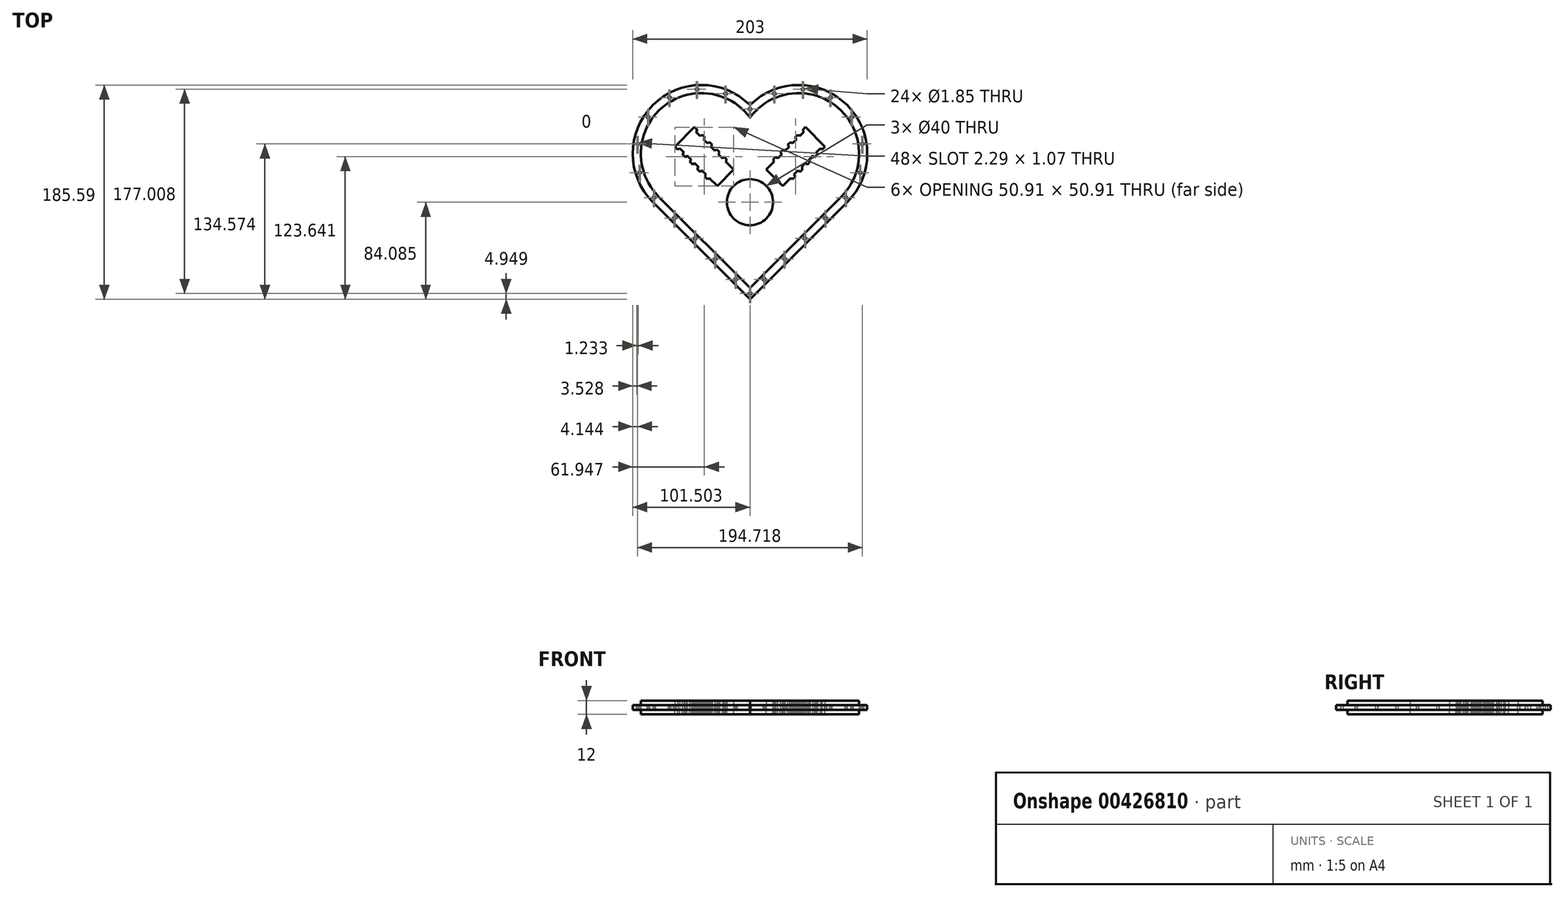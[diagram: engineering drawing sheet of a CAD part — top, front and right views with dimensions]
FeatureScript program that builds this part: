
annotation { "Feature Type Name" : "Feature", "Feature Type Description" : "" }
export const myFeature = defineFeature(function(context is Context, id is Id, definition is map)
    precondition{}
    {
        {
            var Q0;
            Q0=qCreatedBy(makeId("Top.planeOp"),FACE);
            var sketch = newSketch(context, id + "F0", { "sketchPlane" : qUnion([Q0])});
            skArc(sketch, "E0", {"start": v(87.8, -88.57) * mm, "mid": v(87.8, -4.49) * mm, "end": v(3.72, -4.49) * mm});
            skArc(sketch, "E1.MirrorCS", {"start": v(-80.36, -88.57) * mm, "mid": v(-80.36, -4.49) * mm, "end": v(3.72, -4.49) * mm});
            skLineSegment(sketch, "E2", {"start": v(87.8, -88.57) * mm, "end": v(3.72, -172.66) * mm});
            skLineSegment(sketch, "E3", {"start": v(3.72, -172.66) * mm, "end": v(-80.36, -88.57) * mm});
            skCircle(sketch, "E4", {"center": v(3.72, -7.99) * mm, "radius": 0.93 * mm});
            skArc(sketch, "E5", {"start": v(3.64, -6.94) * mm, "mid": v(2.67, -7.99) * mm, "end": v(3.64, -9.04) * mm});
            skArc(sketch, "E6.trimOffspring", {"start": v(3.8, -9.04) * mm, "mid": v(4.77, -7.99) * mm, "end": v(3.8, -6.94) * mm});
            skArc(sketch, "E7.0", {"start": v(3.63, -6.84) * mm, "mid": v(2.57, -7.99) * mm, "end": v(3.63, -9.14) * mm});
            skArc(sketch, "E8.0", {"start": v(3.81, -9.14) * mm, "mid": v(4.87, -7.99) * mm, "end": v(3.81, -6.84) * mm});
            skLineSegment(sketch, "E9", {"start": v(3.8, -9.04) * mm, "end": v(3.81, -9.14) * mm});
            skLineSegment(sketch, "E10", {"start": v(3.64, -9.04) * mm, "end": v(3.63, -9.14) * mm});
            skLineSegment(sketch, "E11", {"start": v(3.63, -6.84) * mm, "end": v(3.64, -6.94) * mm});
            skLineSegment(sketch, "E12", {"start": v(3.81, -6.84) * mm, "end": v(3.8, -6.94) * mm});
            skCircle(sketch, "E13", {"center": v(24.85, 5.37) * mm, "radius": 0.93 * mm});
            skArc(sketch, "E14", {"start": v(24.77, 6.42) * mm, "mid": v(23.8, 5.37) * mm, "end": v(24.77, 4.32) * mm});
            skArc(sketch, "E15.trimOffspring", {"start": v(24.94, 4.32) * mm, "mid": v(25.9, 5.37) * mm, "end": v(24.94, 6.42) * mm});
            skArc(sketch, "E16.0", {"start": v(24.76, 6.52) * mm, "mid": v(23.7, 5.37) * mm, "end": v(24.76, 4.22) * mm});
            skArc(sketch, "E17.0", {"start": v(24.94, 4.22) * mm, "mid": v(26, 5.37) * mm, "end": v(24.94, 6.52) * mm});
            skLineSegment(sketch, "E18", {"start": v(24.94, 4.32) * mm, "end": v(24.94, 4.22) * mm});
            skLineSegment(sketch, "E19", {"start": v(24.77, 4.32) * mm, "end": v(24.76, 4.22) * mm});
            skLineSegment(sketch, "E20", {"start": v(24.76, 6.52) * mm, "end": v(24.77, 6.42) * mm});
            skLineSegment(sketch, "E21", {"start": v(24.94, 6.52) * mm, "end": v(24.94, 6.42) * mm});
            skCircle(sketch, "E22", {"center": v(49.54, 9.3) * mm, "radius": 0.93 * mm});
            skArc(sketch, "E23", {"start": v(49.46, 10.34) * mm, "mid": v(48.5, 9.3) * mm, "end": v(49.46, 8.25) * mm});
            skArc(sketch, "E24.trimOffspring", {"start": v(49.63, 8.25) * mm, "mid": v(50.6, 9.3) * mm, "end": v(49.63, 10.34) * mm});
            skArc(sketch, "E25.0", {"start": v(49.45, 10.44) * mm, "mid": v(48.4, 9.3) * mm, "end": v(49.45, 8.15) * mm});
            skArc(sketch, "E26.0", {"start": v(49.63, 8.15) * mm, "mid": v(50.7, 9.3) * mm, "end": v(49.63, 10.44) * mm});
            skLineSegment(sketch, "E27", {"start": v(49.63, 8.25) * mm, "end": v(49.63, 8.15) * mm});
            skLineSegment(sketch, "E28", {"start": v(49.46, 8.25) * mm, "end": v(49.45, 8.15) * mm});
            skLineSegment(sketch, "E29", {"start": v(49.45, 10.44) * mm, "end": v(49.46, 10.34) * mm});
            skLineSegment(sketch, "E30", {"start": v(49.63, 10.44) * mm, "end": v(49.63, 10.34) * mm});
            skCircle(sketch, "E31", {"center": v(73.48, 2.08) * mm, "radius": 0.93 * mm});
            skArc(sketch, "E32", {"start": v(73.4, 3.13) * mm, "mid": v(72.43, 2.08) * mm, "end": v(73.4, 1.03) * mm});
            skArc(sketch, "E33.trimOffspring", {"start": v(73.56, 1.03) * mm, "mid": v(74.53, 2.08) * mm, "end": v(73.56, 3.13) * mm});
            skArc(sketch, "E34.0", {"start": v(73.39, 3.23) * mm, "mid": v(72.33, 2.08) * mm, "end": v(73.39, 0.93) * mm});
            skArc(sketch, "E35.0", {"start": v(73.57, 0.93) * mm, "mid": v(74.63, 2.08) * mm, "end": v(73.57, 3.23) * mm});
            skLineSegment(sketch, "E36", {"start": v(73.56, 1.03) * mm, "end": v(73.57, 0.93) * mm});
            skLineSegment(sketch, "E37", {"start": v(73.4, 1.03) * mm, "end": v(73.39, 0.93) * mm});
            skLineSegment(sketch, "E38", {"start": v(73.39, 3.23) * mm, "end": v(73.4, 3.13) * mm});
            skLineSegment(sketch, "E39", {"start": v(73.57, 3.23) * mm, "end": v(73.56, 3.13) * mm});
            skCircle(sketch, "E40", {"center": v(91.88, -14.84) * mm, "radius": 0.93 * mm});
            skArc(sketch, "E41", {"start": v(91.8, -13.8) * mm, "mid": v(90.83, -14.84) * mm, "end": v(91.8, -15.89) * mm});
            skArc(sketch, "E42.trimOffspring", {"start": v(91.97, -15.89) * mm, "mid": v(92.93, -14.84) * mm, "end": v(91.97, -13.8) * mm});
            skArc(sketch, "E43.0", {"start": v(91.8, -13.7) * mm, "mid": v(90.73, -14.84) * mm, "end": v(91.8, -15.99) * mm});
            skArc(sketch, "E44.0", {"start": v(91.97, -15.99) * mm, "mid": v(93.03, -14.84) * mm, "end": v(91.97, -13.7) * mm});
            skLineSegment(sketch, "E45", {"start": v(91.97, -15.89) * mm, "end": v(91.97, -15.99) * mm});
            skLineSegment(sketch, "E46", {"start": v(91.8, -15.89) * mm, "end": v(91.8, -15.99) * mm});
            skLineSegment(sketch, "E47", {"start": v(91.8, -13.7) * mm, "end": v(91.8, -13.8) * mm});
            skLineSegment(sketch, "E48", {"start": v(91.97, -13.7) * mm, "end": v(91.97, -13.8) * mm});
            skCircle(sketch, "E49", {"center": v(101.08, -38.09) * mm, "radius": 0.93 * mm});
            skArc(sketch, "E50", {"start": v(101, -37.04) * mm, "mid": v(100.03, -38.09) * mm, "end": v(101, -39.13) * mm});
            skArc(sketch, "E51.trimOffspring", {"start": v(101.16, -39.13) * mm, "mid": v(102.13, -38.09) * mm, "end": v(101.16, -37.04) * mm});
            skArc(sketch, "E52.0", {"start": v(101, -36.94) * mm, "mid": v(99.93, -38.09) * mm, "end": v(101, -39.23) * mm});
            skArc(sketch, "E53.0", {"start": v(101.17, -39.23) * mm, "mid": v(102.23, -38.09) * mm, "end": v(101.17, -36.94) * mm});
            skLineSegment(sketch, "E54", {"start": v(101.16, -39.13) * mm, "end": v(101.17, -39.23) * mm});
            skLineSegment(sketch, "E55", {"start": v(101, -39.13) * mm, "end": v(101, -39.23) * mm});
            skLineSegment(sketch, "E56", {"start": v(101, -36.94) * mm, "end": v(101, -37.04) * mm});
            skLineSegment(sketch, "E57", {"start": v(101.17, -36.94) * mm, "end": v(101.16, -37.04) * mm});
            skCircle(sketch, "E58", {"center": v(99.24, -63.02) * mm, "radius": 0.93 * mm});
            skArc(sketch, "E59", {"start": v(99.16, -61.97) * mm, "mid": v(98.19, -63.02) * mm, "end": v(99.16, -64.06) * mm});
            skArc(sketch, "E60.trimOffspring", {"start": v(99.32, -64.06) * mm, "mid": v(100.29, -63.02) * mm, "end": v(99.32, -61.97) * mm});
            skArc(sketch, "E61.0", {"start": v(99.15, -61.87) * mm, "mid": v(98.09, -63.02) * mm, "end": v(99.15, -64.16) * mm});
            skArc(sketch, "E62.0", {"start": v(99.33, -64.16) * mm, "mid": v(100.39, -63.02) * mm, "end": v(99.33, -61.87) * mm});
            skLineSegment(sketch, "E63", {"start": v(99.32, -64.06) * mm, "end": v(99.33, -64.16) * mm});
            skLineSegment(sketch, "E64", {"start": v(99.16, -64.06) * mm, "end": v(99.15, -64.16) * mm});
            skLineSegment(sketch, "E65", {"start": v(99.15, -61.87) * mm, "end": v(99.16, -61.97) * mm});
            skLineSegment(sketch, "E66", {"start": v(99.33, -61.87) * mm, "end": v(99.32, -61.97) * mm});
            skCircle(sketch, "E67", {"center": v(86.72, -84.66) * mm, "radius": 0.93 * mm});
            skArc(sketch, "E68", {"start": v(86.64, -83.61) * mm, "mid": v(85.67, -84.66) * mm, "end": v(86.64, -85.7) * mm});
            skArc(sketch, "E69.trimOffspring", {"start": v(86.8, -85.7) * mm, "mid": v(87.77, -84.66) * mm, "end": v(86.8, -83.61) * mm});
            skArc(sketch, "E70.0", {"start": v(86.63, -83.51) * mm, "mid": v(85.57, -84.66) * mm, "end": v(86.63, -85.8) * mm});
            skArc(sketch, "E71.0", {"start": v(86.81, -85.8) * mm, "mid": v(87.87, -84.66) * mm, "end": v(86.81, -83.51) * mm});
            skLineSegment(sketch, "E72", {"start": v(86.8, -85.7) * mm, "end": v(86.81, -85.8) * mm});
            skLineSegment(sketch, "E73", {"start": v(86.64, -85.7) * mm, "end": v(86.63, -85.8) * mm});
            skLineSegment(sketch, "E74", {"start": v(86.63, -83.51) * mm, "end": v(86.64, -83.61) * mm});
            skLineSegment(sketch, "E75", {"start": v(86.81, -83.51) * mm, "end": v(86.8, -83.61) * mm});
            skCircle(sketch, "E76", {"center": v(69.07, -102.36) * mm, "radius": 0.93 * mm});
            skArc(sketch, "E77", {"start": v(68.99, -101.32) * mm, "mid": v(68.02, -102.36) * mm, "end": v(68.99, -103.4) * mm});
            skArc(sketch, "E78.trimOffspring", {"start": v(69.15, -103.4) * mm, "mid": v(70.12, -102.36) * mm, "end": v(69.15, -101.32) * mm});
            skArc(sketch, "E79.0", {"start": v(68.98, -101.22) * mm, "mid": v(67.92, -102.36) * mm, "end": v(68.98, -103.5) * mm});
            skArc(sketch, "E80.0", {"start": v(69.16, -103.5) * mm, "mid": v(70.22, -102.36) * mm, "end": v(69.16, -101.22) * mm});
            skLineSegment(sketch, "E81", {"start": v(69.15, -103.4) * mm, "end": v(69.16, -103.5) * mm});
            skLineSegment(sketch, "E82", {"start": v(68.99, -103.4) * mm, "end": v(68.98, -103.5) * mm});
            skLineSegment(sketch, "E83", {"start": v(68.98, -101.22) * mm, "end": v(68.99, -101.32) * mm});
            skLineSegment(sketch, "E84", {"start": v(69.16, -101.22) * mm, "end": v(69.15, -101.32) * mm});
            skCircle(sketch, "E85", {"center": v(51.4, -120.04) * mm, "radius": 0.93 * mm});
            skArc(sketch, "E86", {"start": v(51.31, -119) * mm, "mid": v(50.34, -120.04) * mm, "end": v(51.31, -121.09) * mm});
            skArc(sketch, "E87.trimOffspring", {"start": v(51.48, -121.09) * mm, "mid": v(52.44, -120.04) * mm, "end": v(51.48, -119) * mm});
            skArc(sketch, "E88.0", {"start": v(51.3, -118.9) * mm, "mid": v(50.24, -120.04) * mm, "end": v(51.3, -121.19) * mm});
            skArc(sketch, "E89.0", {"start": v(51.48, -121.19) * mm, "mid": v(52.54, -120.04) * mm, "end": v(51.48, -118.9) * mm});
            skLineSegment(sketch, "E90", {"start": v(51.48, -121.09) * mm, "end": v(51.48, -121.19) * mm});
            skLineSegment(sketch, "E91", {"start": v(51.31, -121.09) * mm, "end": v(51.3, -121.19) * mm});
            skLineSegment(sketch, "E92", {"start": v(51.3, -118.9) * mm, "end": v(51.31, -119) * mm});
            skLineSegment(sketch, "E93", {"start": v(51.48, -118.9) * mm, "end": v(51.48, -119) * mm});
            skCircle(sketch, "E94", {"center": v(33.72, -137.72) * mm, "radius": 0.93 * mm});
            skArc(sketch, "E95", {"start": v(33.63, -136.67) * mm, "mid": v(32.67, -137.72) * mm, "end": v(33.63, -138.76) * mm});
            skArc(sketch, "E96.trimOffspring", {"start": v(33.8, -138.76) * mm, "mid": v(34.77, -137.72) * mm, "end": v(33.8, -136.67) * mm});
            skArc(sketch, "E97.0", {"start": v(33.63, -136.57) * mm, "mid": v(32.57, -137.72) * mm, "end": v(33.63, -138.86) * mm});
            skArc(sketch, "E98.0", {"start": v(33.8, -138.86) * mm, "mid": v(34.87, -137.72) * mm, "end": v(33.8, -136.57) * mm});
            skLineSegment(sketch, "E99", {"start": v(33.8, -138.76) * mm, "end": v(33.8, -138.86) * mm});
            skLineSegment(sketch, "E100", {"start": v(33.63, -138.76) * mm, "end": v(33.63, -138.86) * mm});
            skLineSegment(sketch, "E101", {"start": v(33.63, -136.57) * mm, "end": v(33.63, -136.67) * mm});
            skLineSegment(sketch, "E102", {"start": v(33.8, -136.57) * mm, "end": v(33.8, -136.67) * mm});
            skCircle(sketch, "E103", {"center": v(16.04, -155.4) * mm, "radius": 0.93 * mm});
            skArc(sketch, "E104", {"start": v(15.96, -154.35) * mm, "mid": v(14.99, -155.4) * mm, "end": v(15.96, -156.44) * mm});
            skArc(sketch, "E105.trimOffspring", {"start": v(16.12, -156.44) * mm, "mid": v(17.09, -155.4) * mm, "end": v(16.12, -154.35) * mm});
            skArc(sketch, "E106.0", {"start": v(15.95, -154.25) * mm, "mid": v(14.89, -155.4) * mm, "end": v(15.95, -156.54) * mm});
            skArc(sketch, "E107.0", {"start": v(16.13, -156.54) * mm, "mid": v(17.19, -155.4) * mm, "end": v(16.13, -154.25) * mm});
            skLineSegment(sketch, "E108", {"start": v(16.12, -156.44) * mm, "end": v(16.13, -156.54) * mm});
            skLineSegment(sketch, "E109", {"start": v(15.96, -156.44) * mm, "end": v(15.95, -156.54) * mm});
            skLineSegment(sketch, "E110", {"start": v(15.95, -154.25) * mm, "end": v(15.96, -154.35) * mm});
            skLineSegment(sketch, "E111", {"start": v(16.13, -154.25) * mm, "end": v(16.12, -154.35) * mm});
            skCircle(sketch, "E112", {"center": v(3.72, -167.71) * mm, "radius": 0.93 * mm});
            skArc(sketch, "E113", {"start": v(3.64, -166.66) * mm, "mid": v(2.67, -167.71) * mm, "end": v(3.64, -168.76) * mm});
            skArc(sketch, "E114.trimOffspring", {"start": v(3.8, -168.76) * mm, "mid": v(4.77, -167.71) * mm, "end": v(3.8, -166.66) * mm});
            skArc(sketch, "E115.0", {"start": v(3.63, -166.56) * mm, "mid": v(2.57, -167.71) * mm, "end": v(3.63, -168.86) * mm});
            skArc(sketch, "E116.0", {"start": v(3.81, -168.86) * mm, "mid": v(4.87, -167.71) * mm, "end": v(3.81, -166.56) * mm});
            skLineSegment(sketch, "E117", {"start": v(3.8, -168.76) * mm, "end": v(3.81, -168.86) * mm});
            skLineSegment(sketch, "E118", {"start": v(3.64, -168.76) * mm, "end": v(3.63, -168.86) * mm});
            skLineSegment(sketch, "E119", {"start": v(3.63, -166.56) * mm, "end": v(3.64, -166.66) * mm});
            skLineSegment(sketch, "E120", {"start": v(3.81, -166.56) * mm, "end": v(3.8, -166.66) * mm});
            skLineSegment(sketch, "E121.MirrorCS", {"start": v(-17.5, 4.32) * mm, "end": v(-17.5, 4.22) * mm});
            skLineSegment(sketch, "E122.MirrorCS", {"start": v(-17.32, 4.32) * mm, "end": v(-17.32, 4.22) * mm});
            skLineSegment(sketch, "E123.MirrorCS", {"start": v(-17.5, 6.52) * mm, "end": v(-17.5, 6.42) * mm});
            skLineSegment(sketch, "E124.MirrorCS", {"start": v(-17.32, 6.52) * mm, "end": v(-17.32, 6.42) * mm});
            skArc(sketch, "E125.MirrorCS", {"start": v(-17.5, 4.22) * mm, "mid": v(-18.56, 5.37) * mm, "end": v(-17.5, 6.52) * mm});
            skArc(sketch, "E126.MirrorCS", {"start": v(-17.32, 6.42) * mm, "mid": v(-16.36, 5.37) * mm, "end": v(-17.32, 4.32) * mm});
            skArc(sketch, "E127.MirrorCS", {"start": v(-17.5, 4.32) * mm, "mid": v(-18.46, 5.37) * mm, "end": v(-17.5, 6.42) * mm});
            skCircle(sketch, "E128.MirrorC", {"center": v(-17.4, 5.37) * mm, "radius": 0.93 * mm});
            skArc(sketch, "E129.MirrorCS", {"start": v(-17.32, 6.52) * mm, "mid": v(-16.26, 5.37) * mm, "end": v(-17.32, 4.22) * mm});
            skLineSegment(sketch, "E130.MirrorCS", {"start": v(-42.19, 10.44) * mm, "end": v(-42.18, 10.34) * mm});
            skLineSegment(sketch, "E131.MirrorCS", {"start": v(-42.18, 8.25) * mm, "end": v(-42.19, 8.15) * mm});
            skLineSegment(sketch, "E132.MirrorCS", {"start": v(-42, 10.44) * mm, "end": v(-42.01, 10.34) * mm});
            skLineSegment(sketch, "E133.MirrorCS", {"start": v(-42.01, 8.25) * mm, "end": v(-42, 8.15) * mm});
            skCircle(sketch, "E134.MirrorC", {"center": v(-42.1, 9.3) * mm, "radius": 0.93 * mm});
            skArc(sketch, "E135.MirrorCS", {"start": v(-42.18, 8.25) * mm, "mid": v(-43.15, 9.3) * mm, "end": v(-42.18, 10.34) * mm});
            skArc(sketch, "E136.MirrorCS", {"start": v(-42, 10.44) * mm, "mid": v(-40.95, 9.3) * mm, "end": v(-42, 8.15) * mm});
            skArc(sketch, "E137.MirrorCS", {"start": v(-42.19, 8.15) * mm, "mid": v(-43.25, 9.3) * mm, "end": v(-42.19, 10.44) * mm});
            skArc(sketch, "E138.MirrorCS", {"start": v(-42.01, 10.34) * mm, "mid": v(-41.05, 9.3) * mm, "end": v(-42.01, 8.25) * mm});
            skLineSegment(sketch, "E139.MirrorCS", {"start": v(-65.94, 3.23) * mm, "end": v(-65.95, 3.13) * mm});
            skLineSegment(sketch, "E140.MirrorCS", {"start": v(-66.12, 3.23) * mm, "end": v(-66.12, 3.13) * mm});
            skLineSegment(sketch, "E141.MirrorCS", {"start": v(-66.12, 1.03) * mm, "end": v(-66.12, 0.93) * mm});
            skLineSegment(sketch, "E142.MirrorCS", {"start": v(-65.95, 1.03) * mm, "end": v(-65.94, 0.93) * mm});
            skArc(sketch, "E143.MirrorCS", {"start": v(-65.94, 3.23) * mm, "mid": v(-64.88, 2.08) * mm, "end": v(-65.94, 0.93) * mm});
            skArc(sketch, "E144.MirrorCS", {"start": v(-66.12, 1.03) * mm, "mid": v(-67.08, 2.08) * mm, "end": v(-66.12, 3.13) * mm});
            skArc(sketch, "E145.MirrorCS", {"start": v(-66.12, 0.93) * mm, "mid": v(-67.18, 2.08) * mm, "end": v(-66.12, 3.23) * mm});
            skCircle(sketch, "E146.MirrorC", {"center": v(-66.03, 2.08) * mm, "radius": 0.93 * mm});
            skArc(sketch, "E147.MirrorCS", {"start": v(-65.95, 3.13) * mm, "mid": v(-64.98, 2.08) * mm, "end": v(-65.95, 1.03) * mm});
            skLineSegment(sketch, "E148.MirrorCS", {"start": v(-84.35, -13.7) * mm, "end": v(-84.35, -13.8) * mm});
            skLineSegment(sketch, "E149.MirrorCS", {"start": v(-84.35, -15.89) * mm, "end": v(-84.35, -15.99) * mm});
            skLineSegment(sketch, "E150.MirrorCS", {"start": v(-84.53, -13.7) * mm, "end": v(-84.52, -13.8) * mm});
            skLineSegment(sketch, "E151.MirrorCS", {"start": v(-84.52, -15.89) * mm, "end": v(-84.53, -15.99) * mm});
            skArc(sketch, "E152.MirrorCS", {"start": v(-84.35, -13.8) * mm, "mid": v(-83.39, -14.84) * mm, "end": v(-84.35, -15.89) * mm});
            skCircle(sketch, "E153.MirrorC", {"center": v(-84.44, -14.84) * mm, "radius": 0.93 * mm});
            skArc(sketch, "E154.MirrorCS", {"start": v(-84.53, -15.99) * mm, "mid": v(-85.59, -14.84) * mm, "end": v(-84.53, -13.7) * mm});
            skArc(sketch, "E155.MirrorCS", {"start": v(-84.35, -13.7) * mm, "mid": v(-83.29, -14.84) * mm, "end": v(-84.35, -15.99) * mm});
            skArc(sketch, "E156.MirrorCS", {"start": v(-84.52, -15.89) * mm, "mid": v(-85.49, -14.84) * mm, "end": v(-84.52, -13.8) * mm});
            skLineSegment(sketch, "E157.MirrorCS", {"start": v(-93.55, -36.94) * mm, "end": v(-93.55, -37.04) * mm});
            skLineSegment(sketch, "E158.MirrorCS", {"start": v(-93.55, -39.13) * mm, "end": v(-93.55, -39.23) * mm});
            skLineSegment(sketch, "E159.MirrorCS", {"start": v(-93.72, -39.13) * mm, "end": v(-93.73, -39.23) * mm});
            skLineSegment(sketch, "E160.MirrorCS", {"start": v(-93.73, -36.94) * mm, "end": v(-93.72, -37.04) * mm});
            skArc(sketch, "E161.MirrorCS", {"start": v(-93.55, -37.04) * mm, "mid": v(-92.59, -38.09) * mm, "end": v(-93.55, -39.13) * mm});
            skArc(sketch, "E162.MirrorCS", {"start": v(-93.72, -39.13) * mm, "mid": v(-94.69, -38.09) * mm, "end": v(-93.72, -37.04) * mm});
            skCircle(sketch, "E163.MirrorC", {"center": v(-93.64, -38.09) * mm, "radius": 0.93 * mm});
            skArc(sketch, "E164.MirrorCS", {"start": v(-93.73, -39.23) * mm, "mid": v(-94.79, -38.09) * mm, "end": v(-93.73, -36.94) * mm});
            skArc(sketch, "E165.MirrorCS", {"start": v(-93.55, -36.94) * mm, "mid": v(-92.49, -38.09) * mm, "end": v(-93.55, -39.23) * mm});
            skLineSegment(sketch, "E166.MirrorCS", {"start": v(-91.71, -64.06) * mm, "end": v(-91.7, -64.16) * mm});
            skLineSegment(sketch, "E167.MirrorCS", {"start": v(-91.88, -61.87) * mm, "end": v(-91.88, -61.97) * mm});
            skLineSegment(sketch, "E168.MirrorCS", {"start": v(-91.7, -61.87) * mm, "end": v(-91.71, -61.97) * mm});
            skLineSegment(sketch, "E169.MirrorCS", {"start": v(-91.88, -64.06) * mm, "end": v(-91.88, -64.16) * mm});
            skArc(sketch, "E170.MirrorCS", {"start": v(-91.88, -64.16) * mm, "mid": v(-92.94, -63.02) * mm, "end": v(-91.88, -61.87) * mm});
            skArc(sketch, "E171.MirrorCS", {"start": v(-91.71, -61.97) * mm, "mid": v(-90.74, -63.02) * mm, "end": v(-91.71, -64.06) * mm});
            skArc(sketch, "E172.MirrorCS", {"start": v(-91.88, -64.06) * mm, "mid": v(-92.84, -63.02) * mm, "end": v(-91.88, -61.97) * mm});
            skCircle(sketch, "E173.MirrorC", {"center": v(-91.8, -63.02) * mm, "radius": 0.93 * mm});
            skArc(sketch, "E174.MirrorCS", {"start": v(-91.7, -61.87) * mm, "mid": v(-90.64, -63.02) * mm, "end": v(-91.7, -64.16) * mm});
            skLineSegment(sketch, "E175.MirrorCS", {"start": v(-79.2, -85.7) * mm, "end": v(-79.19, -85.8) * mm});
            skLineSegment(sketch, "E176.MirrorCS", {"start": v(-79.36, -85.7) * mm, "end": v(-79.37, -85.8) * mm});
            skLineSegment(sketch, "E177.MirrorCS", {"start": v(-79.37, -83.51) * mm, "end": v(-79.36, -83.61) * mm});
            skLineSegment(sketch, "E178.MirrorCS", {"start": v(-79.19, -83.51) * mm, "end": v(-79.2, -83.61) * mm});
            skArc(sketch, "E179.MirrorCS", {"start": v(-79.37, -85.8) * mm, "mid": v(-80.43, -84.66) * mm, "end": v(-79.37, -83.51) * mm});
            skArc(sketch, "E180.MirrorCS", {"start": v(-79.19, -83.51) * mm, "mid": v(-78.13, -84.66) * mm, "end": v(-79.19, -85.8) * mm});
            skArc(sketch, "E181.MirrorCS", {"start": v(-79.2, -83.61) * mm, "mid": v(-78.23, -84.66) * mm, "end": v(-79.2, -85.7) * mm});
            skCircle(sketch, "E182.MirrorC", {"center": v(-79.28, -84.66) * mm, "radius": 0.93 * mm});
            skArc(sketch, "E183.MirrorCS", {"start": v(-79.36, -85.7) * mm, "mid": v(-80.33, -84.66) * mm, "end": v(-79.36, -83.61) * mm});
            skLineSegment(sketch, "E184.MirrorCS", {"start": v(-61.7, -103.4) * mm, "end": v(-61.72, -103.5) * mm});
            skLineSegment(sketch, "E185.MirrorCS", {"start": v(-61.54, -103.4) * mm, "end": v(-61.53, -103.5) * mm});
            skLineSegment(sketch, "E186.MirrorCS", {"start": v(-61.72, -101.22) * mm, "end": v(-61.7, -101.32) * mm});
            skLineSegment(sketch, "E187.MirrorCS", {"start": v(-61.53, -101.22) * mm, "end": v(-61.54, -101.32) * mm});
            skArc(sketch, "E188.MirrorCS", {"start": v(-61.54, -101.32) * mm, "mid": v(-60.58, -102.36) * mm, "end": v(-61.54, -103.4) * mm});
            skArc(sketch, "E189.MirrorCS", {"start": v(-61.72, -103.5) * mm, "mid": v(-62.78, -102.36) * mm, "end": v(-61.72, -101.22) * mm});
            skArc(sketch, "E190.MirrorCS", {"start": v(-61.7, -103.4) * mm, "mid": v(-62.68, -102.36) * mm, "end": v(-61.7, -101.32) * mm});
            skCircle(sketch, "E191.MirrorC", {"center": v(-61.63, -102.36) * mm, "radius": 0.93 * mm});
            skArc(sketch, "E192.MirrorCS", {"start": v(-61.53, -101.22) * mm, "mid": v(-60.48, -102.36) * mm, "end": v(-61.53, -103.5) * mm});
            skLineSegment(sketch, "E193.MirrorCS", {"start": v(-43.86, -121.09) * mm, "end": v(-43.86, -121.19) * mm});
            skLineSegment(sketch, "E194.MirrorCS", {"start": v(-44.03, -121.09) * mm, "end": v(-44.04, -121.19) * mm});
            skLineSegment(sketch, "E195.MirrorCS", {"start": v(-44.04, -118.9) * mm, "end": v(-44.03, -119) * mm});
            skLineSegment(sketch, "E196.MirrorCS", {"start": v(-43.86, -118.9) * mm, "end": v(-43.86, -119) * mm});
            skArc(sketch, "E197.MirrorCS", {"start": v(-43.86, -118.9) * mm, "mid": v(-42.8, -120.04) * mm, "end": v(-43.86, -121.19) * mm});
            skArc(sketch, "E198.MirrorCS", {"start": v(-43.86, -119) * mm, "mid": v(-42.9, -120.04) * mm, "end": v(-43.86, -121.09) * mm});
            skArc(sketch, "E199.MirrorCS", {"start": v(-44.03, -121.09) * mm, "mid": v(-45, -120.04) * mm, "end": v(-44.03, -119) * mm});
            skArc(sketch, "E200.MirrorCS", {"start": v(-44.04, -121.19) * mm, "mid": v(-45.1, -120.04) * mm, "end": v(-44.04, -118.9) * mm});
            skCircle(sketch, "E201.MirrorC", {"center": v(-43.95, -120.04) * mm, "radius": 0.93 * mm});
            skLineSegment(sketch, "E202.MirrorCS", {"start": v(-26.36, -136.57) * mm, "end": v(-26.35, -136.67) * mm});
            skLineSegment(sketch, "E203.MirrorCS", {"start": v(-26.35, -138.76) * mm, "end": v(-26.36, -138.86) * mm});
            skLineSegment(sketch, "E204.MirrorCS", {"start": v(-26.19, -138.76) * mm, "end": v(-26.18, -138.86) * mm});
            skLineSegment(sketch, "E205.MirrorCS", {"start": v(-26.18, -136.57) * mm, "end": v(-26.19, -136.67) * mm});
            skArc(sketch, "E206.MirrorCS", {"start": v(-26.19, -136.67) * mm, "mid": v(-25.22, -137.72) * mm, "end": v(-26.19, -138.76) * mm});
            skArc(sketch, "E207.MirrorCS", {"start": v(-26.18, -136.57) * mm, "mid": v(-25.12, -137.72) * mm, "end": v(-26.18, -138.86) * mm});
            skArc(sketch, "E208.MirrorCS", {"start": v(-26.35, -138.76) * mm, "mid": v(-27.32, -137.72) * mm, "end": v(-26.35, -136.67) * mm});
            skArc(sketch, "E209.MirrorCS", {"start": v(-26.36, -138.86) * mm, "mid": v(-27.42, -137.72) * mm, "end": v(-26.36, -136.57) * mm});
            skCircle(sketch, "E210.MirrorC", {"center": v(-26.27, -137.72) * mm, "radius": 0.93 * mm});
            skLineSegment(sketch, "E211.MirrorCS", {"start": v(-8.68, -154.25) * mm, "end": v(-8.67, -154.35) * mm});
            skLineSegment(sketch, "E212.MirrorCS", {"start": v(-8.5, -154.25) * mm, "end": v(-8.5, -154.35) * mm});
            skLineSegment(sketch, "E213.MirrorCS", {"start": v(-8.5, -156.44) * mm, "end": v(-8.5, -156.54) * mm});
            skLineSegment(sketch, "E214.MirrorCS", {"start": v(-8.67, -156.44) * mm, "end": v(-8.68, -156.54) * mm});
            skArc(sketch, "E215.MirrorCS", {"start": v(-8.5, -154.25) * mm, "mid": v(-7.44, -155.4) * mm, "end": v(-8.5, -156.54) * mm});
            skArc(sketch, "E216.MirrorCS", {"start": v(-8.5, -154.35) * mm, "mid": v(-7.54, -155.4) * mm, "end": v(-8.5, -156.44) * mm});
            skCircle(sketch, "E217.MirrorC", {"center": v(-8.6, -155.4) * mm, "radius": 0.93 * mm});
            skArc(sketch, "E218.MirrorCS", {"start": v(-8.68, -156.54) * mm, "mid": v(-9.74, -155.4) * mm, "end": v(-8.68, -154.25) * mm});
            skArc(sketch, "E219.MirrorCS", {"start": v(-8.67, -156.44) * mm, "mid": v(-9.64, -155.4) * mm, "end": v(-8.67, -154.35) * mm});
            skLineSegment(sketch, "E220", {"start": v(3.72, -4.49) * mm, "end": v(3.72, -172.66) * mm, "construction": true});
            skCircle(sketch, "E221", {"center": v(3.72, -88.57) * mm, "radius": 20 * mm});
            skLineSegment(sketch, "E222", {"start": v(-52.8, -32.05) * mm, "end": v(-38.66, -46.2) * mm, "construction": true});
            skLineSegment(sketch, "E223", {"start": v(-57.19, -41.8) * mm, "end": v(-53.47, -45.52) * mm});
            skLineSegment(sketch, "E224", {"start": v(-52.8, -32.05) * mm, "end": v(-59.87, -39.12) * mm});
            skLineSegment(sketch, "E225", {"start": v(-31.59, -67.4) * mm, "end": v(-24.52, -74.48) * mm});
            skLineSegment(sketch, "E226", {"start": v(-59.87, -39.12) * mm, "end": v(-61.29, -40.53) * mm});
            skLineSegment(sketch, "E227", {"start": v(-61.29, -40.53) * mm, "end": v(-58.6, -43.22) * mm});
            skLineSegment(sketch, "E228", {"start": v(-24.52, -74.48) * mm, "end": v(-24.53, -74.48) * mm});
            skLineSegment(sketch, "E229", {"start": v(-57.19, -41.8) * mm, "end": v(-58.6, -43.22) * mm});
            skLineSegment(sketch, "E230", {"start": v(-53.47, -45.52) * mm, "end": v(-54.89, -46.93) * mm});
            skLineSegment(sketch, "E231", {"start": v(-50.79, -48.2) * mm, "end": v(-52.2, -49.62) * mm});
            skLineSegment(sketch, "E232", {"start": v(-31.59, -67.4) * mm, "end": v(-33, -68.82) * mm});
            skLineSegment(sketch, "E233", {"start": v(-34.28, -64.72) * mm, "end": v(-35.7, -66.13) * mm});
            skLineSegment(sketch, "E234", {"start": v(-37.99, -61) * mm, "end": v(-39.4, -62.42) * mm});
            skLineSegment(sketch, "E235", {"start": v(-40.68, -58.32) * mm, "end": v(-42.1, -59.73) * mm});
            skLineSegment(sketch, "E236.trimOffspring", {"start": v(-37.99, -61) * mm, "end": v(-34.28, -64.72) * mm});
            skLineSegment(sketch, "E237.trimOffspring", {"start": v(-50.79, -48.2) * mm, "end": v(-47.08, -51.92) * mm});
            skLineSegment(sketch, "E238", {"start": v(-44.39, -54.6) * mm, "end": v(-45.8, -56.02) * mm});
            skLineSegment(sketch, "E239.trimOffspring", {"start": v(-44.39, -54.6) * mm, "end": v(-40.68, -58.32) * mm});
            skLineSegment(sketch, "E240", {"start": v(-24.52, -74.48) * mm, "end": v(-17.45, -67.4) * mm});
            skLineSegment(sketch, "E241.MirrorCS", {"start": v(-10.38, -60.33) * mm, "end": v(-17.45, -67.4) * mm});
            skLineSegment(sketch, "E242.MirrorCS", {"start": v(-10.38, -60.33) * mm, "end": v(-10.37, -60.33) * mm});
            skLineSegment(sketch, "E243.MirrorCS", {"start": v(-17.45, -53.26) * mm, "end": v(-10.38, -60.33) * mm});
            skLineSegment(sketch, "E244.MirrorCS", {"start": v(-17.45, -53.26) * mm, "end": v(-16.03, -51.85) * mm});
            skLineSegment(sketch, "E245.MirrorCS", {"start": v(-20.13, -50.58) * mm, "end": v(-18.72, -49.16) * mm});
            skLineSegment(sketch, "E246.MirrorCS", {"start": v(-23.85, -46.86) * mm, "end": v(-20.13, -50.58) * mm});
            skLineSegment(sketch, "E247.MirrorCS", {"start": v(-23.85, -46.86) * mm, "end": v(-22.43, -45.45) * mm});
            skLineSegment(sketch, "E248.MirrorCS", {"start": v(-26.53, -44.18) * mm, "end": v(-25.12, -42.76) * mm});
            skLineSegment(sketch, "E249.MirrorCS", {"start": v(-30.25, -40.46) * mm, "end": v(-26.53, -44.18) * mm});
            skLineSegment(sketch, "E250.MirrorCS", {"start": v(-30.25, -40.46) * mm, "end": v(-28.83, -39.05) * mm});
            skLineSegment(sketch, "E251.MirrorCS", {"start": v(-36.65, -34.06) * mm, "end": v(-32.93, -37.78) * mm});
            skLineSegment(sketch, "E252.MirrorCS", {"start": v(-36.65, -34.06) * mm, "end": v(-35.23, -32.65) * mm});
            skLineSegment(sketch, "E253.MirrorCS", {"start": v(-39.33, -31.38) * mm, "end": v(-37.92, -29.96) * mm});
            skLineSegment(sketch, "E254.MirrorCS", {"start": v(-43.04, -27.66) * mm, "end": v(-39.33, -31.38) * mm});
            skLineSegment(sketch, "E255.MirrorCS", {"start": v(-44.32, -23.56) * mm, "end": v(-41.63, -26.25) * mm});
            skLineSegment(sketch, "E256.MirrorCS", {"start": v(-43.04, -27.66) * mm, "end": v(-41.63, -26.25) * mm});
            skLineSegment(sketch, "E257.MirrorCS", {"start": v(-52.8, -32.05) * mm, "end": v(-45.73, -24.98) * mm});
            skLineSegment(sketch, "E258.MirrorCS", {"start": v(-45.73, -24.98) * mm, "end": v(-44.32, -23.56) * mm});
            skLineSegment(sketch, "E259.trimOffspring", {"start": v(-54.89, -46.93) * mm, "end": v(-52.2, -49.62) * mm});
            skLineSegment(sketch, "E260.trimOffspring", {"start": v(-42.1, -59.73) * mm, "end": v(-39.4, -62.42) * mm});
            skLineSegment(sketch, "E261.trimOffspring", {"start": v(-35.7, -66.13) * mm, "end": v(-33, -68.82) * mm});
            skLineSegment(sketch, "E262", {"start": v(-47.08, -51.92) * mm, "end": v(-48.49, -53.33) * mm});
            skLineSegment(sketch, "E263.trimOffspring", {"start": v(-48.49, -53.33) * mm, "end": v(-45.8, -56.02) * mm});
            skLineSegment(sketch, "E264.trimOffspring", {"start": v(-37.92, -29.96) * mm, "end": v(-35.23, -32.65) * mm});
            skLineSegment(sketch, "E265.trimOffspring", {"start": v(-25.12, -42.76) * mm, "end": v(-22.43, -45.45) * mm});
            skLineSegment(sketch, "E266.trimOffspring", {"start": v(-18.72, -49.16) * mm, "end": v(-16.03, -51.85) * mm});
            skLineSegment(sketch, "E267", {"start": v(-32.93, -37.78) * mm, "end": v(-31.52, -36.36) * mm});
            skLineSegment(sketch, "E268.trimOffspring", {"start": v(-31.52, -36.36) * mm, "end": v(-28.83, -39.05) * mm});
            skLineSegment(sketch, "E269.MirrorCS", {"start": v(-80.36, -88.57) * mm, "end": v(87.8, -88.57) * mm, "construction": true});
            skLineSegment(sketch, "E270.MirrorCS", {"start": v(31.96, -74.48) * mm, "end": v(31.97, -74.48) * mm});
            skLineSegment(sketch, "E271.MirrorCS", {"start": v(17.82, -60.33) * mm, "end": v(17.82, -60.33) * mm});
            skLineSegment(sketch, "E272.MirrorCS", {"start": v(68.73, -40.53) * mm, "end": v(66.05, -43.22) * mm});
            skLineSegment(sketch, "E273.MirrorCS", {"start": v(64.63, -41.8) * mm, "end": v(66.05, -43.22) * mm});
            skLineSegment(sketch, "E274.MirrorCS", {"start": v(67.32, -39.12) * mm, "end": v(68.73, -40.53) * mm});
            skLineSegment(sketch, "E275.MirrorCS", {"start": v(39.04, -67.4) * mm, "end": v(40.45, -68.82) * mm});
            skLineSegment(sketch, "E276.MirrorCS", {"start": v(60.92, -45.52) * mm, "end": v(62.34, -46.93) * mm});
            skLineSegment(sketch, "E277.MirrorCS", {"start": v(48.12, -58.32) * mm, "end": v(49.54, -59.73) * mm});
            skLineSegment(sketch, "E278.MirrorCS", {"start": v(41.72, -64.72) * mm, "end": v(43.14, -66.13) * mm});
            skLineSegment(sketch, "E279.MirrorCS", {"start": v(37.7, -40.46) * mm, "end": v(36.28, -39.05) * mm});
            skLineSegment(sketch, "E280.MirrorCS", {"start": v(44.1, -34.06) * mm, "end": v(42.68, -32.65) * mm});
            skLineSegment(sketch, "E281.MirrorCS", {"start": v(58.23, -48.2) * mm, "end": v(59.65, -49.62) * mm});
            skLineSegment(sketch, "E282.MirrorCS", {"start": v(45.36, -29.96) * mm, "end": v(42.68, -32.65) * mm});
            skLineSegment(sketch, "E283.MirrorCS", {"start": v(53.18, -24.98) * mm, "end": v(51.76, -23.56) * mm});
            skLineSegment(sketch, "E284.MirrorCS", {"start": v(43.14, -66.13) * mm, "end": v(40.45, -68.82) * mm});
            skLineSegment(sketch, "E285.MirrorCS", {"start": v(51.76, -23.56) * mm, "end": v(49.08, -26.25) * mm});
            skLineSegment(sketch, "E286.MirrorCS", {"start": v(45.44, -61) * mm, "end": v(41.72, -64.72) * mm});
            skLineSegment(sketch, "E287.MirrorCS", {"start": v(37.7, -40.46) * mm, "end": v(33.98, -44.18) * mm});
            skLineSegment(sketch, "E288.MirrorCS", {"start": v(62.34, -46.93) * mm, "end": v(59.65, -49.62) * mm});
            skLineSegment(sketch, "E289.MirrorCS", {"start": v(33.98, -44.18) * mm, "end": v(32.57, -42.76) * mm});
            skLineSegment(sketch, "E290.MirrorCS", {"start": v(31.3, -46.86) * mm, "end": v(29.88, -45.45) * mm});
            skLineSegment(sketch, "E291.MirrorCS", {"start": v(46.78, -31.38) * mm, "end": v(45.36, -29.96) * mm});
            skLineSegment(sketch, "E292.MirrorCS", {"start": v(40.38, -37.78) * mm, "end": v(38.97, -36.36) * mm});
            skLineSegment(sketch, "E293.MirrorCS", {"start": v(32.57, -42.76) * mm, "end": v(29.88, -45.45) * mm});
            skLineSegment(sketch, "E294.MirrorCS", {"start": v(55.94, -53.33) * mm, "end": v(53.25, -56.02) * mm});
            skLineSegment(sketch, "E295.MirrorCS", {"start": v(50.5, -27.66) * mm, "end": v(49.08, -26.25) * mm});
            skLineSegment(sketch, "E296.MirrorCS", {"start": v(38.97, -36.36) * mm, "end": v(36.28, -39.05) * mm});
            skLineSegment(sketch, "E297.MirrorCS", {"start": v(51.83, -54.6) * mm, "end": v(53.25, -56.02) * mm});
            skLineSegment(sketch, "E298.MirrorCS", {"start": v(45.44, -61) * mm, "end": v(46.85, -62.42) * mm});
            skLineSegment(sketch, "E299.MirrorCS", {"start": v(24.9, -53.26) * mm, "end": v(23.48, -51.85) * mm});
            skLineSegment(sketch, "E300.MirrorCS", {"start": v(49.54, -59.73) * mm, "end": v(46.85, -62.42) * mm});
            skLineSegment(sketch, "E301.MirrorCS", {"start": v(26.17, -49.16) * mm, "end": v(23.48, -51.85) * mm});
            skLineSegment(sketch, "E302.MirrorCS", {"start": v(54.52, -51.92) * mm, "end": v(55.94, -53.33) * mm});
            skLineSegment(sketch, "E303.MirrorCS", {"start": v(27.58, -50.58) * mm, "end": v(26.17, -49.16) * mm});
            skLineSegment(sketch, "E304.MirrorCS", {"start": v(39.04, -67.4) * mm, "end": v(31.96, -74.48) * mm});
            skLineSegment(sketch, "E305.MirrorCS", {"start": v(60.25, -32.05) * mm, "end": v(67.32, -39.12) * mm});
            skLineSegment(sketch, "E306.MirrorCS", {"start": v(60.25, -32.05) * mm, "end": v(53.18, -24.98) * mm});
            skLineSegment(sketch, "E307.MirrorCS", {"start": v(31.96, -74.48) * mm, "end": v(24.9, -67.4) * mm});
            skLineSegment(sketch, "E308.MirrorCS", {"start": v(58.23, -48.2) * mm, "end": v(54.52, -51.92) * mm});
            skLineSegment(sketch, "E309.MirrorCS", {"start": v(64.63, -41.8) * mm, "end": v(60.92, -45.52) * mm});
            skLineSegment(sketch, "E310.MirrorCS", {"start": v(17.82, -60.33) * mm, "end": v(24.9, -67.4) * mm});
            skLineSegment(sketch, "E311.MirrorCS", {"start": v(44.1, -34.06) * mm, "end": v(40.38, -37.78) * mm});
            skLineSegment(sketch, "E312.MirrorCS", {"start": v(24.9, -53.26) * mm, "end": v(17.82, -60.33) * mm});
            skLineSegment(sketch, "E313.MirrorCS", {"start": v(51.83, -54.6) * mm, "end": v(48.12, -58.32) * mm});
            skLineSegment(sketch, "E314.MirrorCS", {"start": v(31.3, -46.86) * mm, "end": v(27.58, -50.58) * mm});
            skLineSegment(sketch, "E315.MirrorCS", {"start": v(50.5, -27.66) * mm, "end": v(46.78, -31.38) * mm});
            skLineSegment(sketch, "E316.MirrorCS", {"start": v(60.25, -32.05) * mm, "end": v(46.1, -46.2) * mm, "construction": true});
            skSolve(sketch);
        }
        {
            var Q0;
            Q0=makeQuery(id+"F0.imprint","IMPRINT",FACE,{"disambiguationData":[TD([[makeQuery(id+"F0.imprint","IMPRINT",EDGE,{"derivedFrom":sQuery(id+"F0.wireOp",EDGE,"E0")}),1.0]])]});
            extrude(context, id + "F1", {"entities" : qUnion([Q0]), "depth" : 4 * mm});
        }
        {
            var Q0;
            Q0=makeQuery(id+"F1.opExtrude","CAP_FACE",FACE,{"disambiguationData":[OSD([sQuery(id+"F0.wireOp",EDGE,"E0"),sQuery(id+"F0.wireOp",EDGE,"E1.MirrorCS"),sQuery(id+"F0.wireOp",EDGE,"E2"),sQuery(id+"F0.wireOp",EDGE,"E3"),sQuery(id+"F0.wireOp",EDGE,"E4"),sQuery(id+"F0.wireOp",EDGE,"E5"),sQuery(id+"F0.wireOp",EDGE,"E6.trimOffspring"),sQuery(id+"F0.wireOp",EDGE,"E7.0"),sQuery(id+"F0.wireOp",EDGE,"E8.0"),sQuery(id+"F0.wireOp",EDGE,"E9"),sQuery(id+"F0.wireOp",EDGE,"E10"),sQuery(id+"F0.wireOp",EDGE,"E11"),sQuery(id+"F0.wireOp",EDGE,"E12"),sQuery(id+"F0.wireOp",EDGE,"E13"),sQuery(id+"F0.wireOp",EDGE,"E14"),sQuery(id+"F0.wireOp",EDGE,"E15.trimOffspring"),sQuery(id+"F0.wireOp",EDGE,"E16.0"),sQuery(id+"F0.wireOp",EDGE,"E17.0"),sQuery(id+"F0.wireOp",EDGE,"E18"),sQuery(id+"F0.wireOp",EDGE,"E19"),sQuery(id+"F0.wireOp",EDGE,"E20"),sQuery(id+"F0.wireOp",EDGE,"E21"),sQuery(id+"F0.wireOp",EDGE,"E22"),sQuery(id+"F0.wireOp",EDGE,"E23"),sQuery(id+"F0.wireOp",EDGE,"E24.trimOffspring"),sQuery(id+"F0.wireOp",EDGE,"E25.0"),sQuery(id+"F0.wireOp",EDGE,"E26.0"),sQuery(id+"F0.wireOp",EDGE,"E27"),sQuery(id+"F0.wireOp",EDGE,"E28"),sQuery(id+"F0.wireOp",EDGE,"E29"),sQuery(id+"F0.wireOp",EDGE,"E30"),sQuery(id+"F0.wireOp",EDGE,"E31"),sQuery(id+"F0.wireOp",EDGE,"E32"),sQuery(id+"F0.wireOp",EDGE,"E33.trimOffspring"),sQuery(id+"F0.wireOp",EDGE,"E34.0"),sQuery(id+"F0.wireOp",EDGE,"E35.0"),sQuery(id+"F0.wireOp",EDGE,"E36"),sQuery(id+"F0.wireOp",EDGE,"E37"),sQuery(id+"F0.wireOp",EDGE,"E38"),sQuery(id+"F0.wireOp",EDGE,"E39"),sQuery(id+"F0.wireOp",EDGE,"E40"),sQuery(id+"F0.wireOp",EDGE,"E41"),sQuery(id+"F0.wireOp",EDGE,"E42.trimOffspring"),sQuery(id+"F0.wireOp",EDGE,"E43.0"),sQuery(id+"F0.wireOp",EDGE,"E44.0"),sQuery(id+"F0.wireOp",EDGE,"E45"),sQuery(id+"F0.wireOp",EDGE,"E46"),sQuery(id+"F0.wireOp",EDGE,"E47"),sQuery(id+"F0.wireOp",EDGE,"E48"),sQuery(id+"F0.wireOp",EDGE,"E49"),sQuery(id+"F0.wireOp",EDGE,"E50"),sQuery(id+"F0.wireOp",EDGE,"E51.trimOffspring"),sQuery(id+"F0.wireOp",EDGE,"E52.0"),sQuery(id+"F0.wireOp",EDGE,"E53.0"),sQuery(id+"F0.wireOp",EDGE,"E54"),sQuery(id+"F0.wireOp",EDGE,"E55"),sQuery(id+"F0.wireOp",EDGE,"E56"),sQuery(id+"F0.wireOp",EDGE,"E57"),sQuery(id+"F0.wireOp",EDGE,"E58"),sQuery(id+"F0.wireOp",EDGE,"E59"),sQuery(id+"F0.wireOp",EDGE,"E60.trimOffspring"),sQuery(id+"F0.wireOp",EDGE,"E61.0"),sQuery(id+"F0.wireOp",EDGE,"E62.0"),sQuery(id+"F0.wireOp",EDGE,"E63"),sQuery(id+"F0.wireOp",EDGE,"E64"),sQuery(id+"F0.wireOp",EDGE,"E65"),sQuery(id+"F0.wireOp",EDGE,"E66"),sQuery(id+"F0.wireOp",EDGE,"E67"),sQuery(id+"F0.wireOp",EDGE,"E68"),sQuery(id+"F0.wireOp",EDGE,"E69.trimOffspring"),sQuery(id+"F0.wireOp",EDGE,"E70.0"),sQuery(id+"F0.wireOp",EDGE,"E71.0"),sQuery(id+"F0.wireOp",EDGE,"E72"),sQuery(id+"F0.wireOp",EDGE,"E73"),sQuery(id+"F0.wireOp",EDGE,"E74"),sQuery(id+"F0.wireOp",EDGE,"E75"),sQuery(id+"F0.wireOp",EDGE,"E76"),sQuery(id+"F0.wireOp",EDGE,"E77"),sQuery(id+"F0.wireOp",EDGE,"E78.trimOffspring"),sQuery(id+"F0.wireOp",EDGE,"E79.0"),sQuery(id+"F0.wireOp",EDGE,"E80.0"),sQuery(id+"F0.wireOp",EDGE,"E81"),sQuery(id+"F0.wireOp",EDGE,"E82"),sQuery(id+"F0.wireOp",EDGE,"E83"),sQuery(id+"F0.wireOp",EDGE,"E84"),sQuery(id+"F0.wireOp",EDGE,"E85"),sQuery(id+"F0.wireOp",EDGE,"E86"),sQuery(id+"F0.wireOp",EDGE,"E87.trimOffspring"),sQuery(id+"F0.wireOp",EDGE,"E88.0"),sQuery(id+"F0.wireOp",EDGE,"E89.0"),sQuery(id+"F0.wireOp",EDGE,"E90"),sQuery(id+"F0.wireOp",EDGE,"E91"),sQuery(id+"F0.wireOp",EDGE,"E92"),sQuery(id+"F0.wireOp",EDGE,"E93"),sQuery(id+"F0.wireOp",EDGE,"E94"),sQuery(id+"F0.wireOp",EDGE,"E95"),sQuery(id+"F0.wireOp",EDGE,"E96.trimOffspring"),sQuery(id+"F0.wireOp",EDGE,"E97.0"),sQuery(id+"F0.wireOp",EDGE,"E98.0"),sQuery(id+"F0.wireOp",EDGE,"E99"),sQuery(id+"F0.wireOp",EDGE,"E100"),sQuery(id+"F0.wireOp",EDGE,"E101"),sQuery(id+"F0.wireOp",EDGE,"E102"),sQuery(id+"F0.wireOp",EDGE,"E103"),sQuery(id+"F0.wireOp",EDGE,"E104"),sQuery(id+"F0.wireOp",EDGE,"E105.trimOffspring"),sQuery(id+"F0.wireOp",EDGE,"E106.0"),sQuery(id+"F0.wireOp",EDGE,"E107.0"),sQuery(id+"F0.wireOp",EDGE,"E108"),sQuery(id+"F0.wireOp",EDGE,"E109"),sQuery(id+"F0.wireOp",EDGE,"E110"),sQuery(id+"F0.wireOp",EDGE,"E111"),sQuery(id+"F0.wireOp",EDGE,"E112"),sQuery(id+"F0.wireOp",EDGE,"E113"),sQuery(id+"F0.wireOp",EDGE,"E114.trimOffspring"),sQuery(id+"F0.wireOp",EDGE,"E115.0"),sQuery(id+"F0.wireOp",EDGE,"E116.0"),sQuery(id+"F0.wireOp",EDGE,"E117"),sQuery(id+"F0.wireOp",EDGE,"E118"),sQuery(id+"F0.wireOp",EDGE,"E119"),sQuery(id+"F0.wireOp",EDGE,"E120"),sQuery(id+"F0.wireOp",EDGE,"E121.MirrorCS"),sQuery(id+"F0.wireOp",EDGE,"E122.MirrorCS"),sQuery(id+"F0.wireOp",EDGE,"E123.MirrorCS"),sQuery(id+"F0.wireOp",EDGE,"E124.MirrorCS"),sQuery(id+"F0.wireOp",EDGE,"E125.MirrorCS"),sQuery(id+"F0.wireOp",EDGE,"E126.MirrorCS"),sQuery(id+"F0.wireOp",EDGE,"E127.MirrorCS"),sQuery(id+"F0.wireOp",EDGE,"E128.MirrorC"),sQuery(id+"F0.wireOp",EDGE,"E129.MirrorCS"),sQuery(id+"F0.wireOp",EDGE,"E130.MirrorCS"),sQuery(id+"F0.wireOp",EDGE,"E131.MirrorCS"),sQuery(id+"F0.wireOp",EDGE,"E132.MirrorCS"),sQuery(id+"F0.wireOp",EDGE,"E133.MirrorCS"),sQuery(id+"F0.wireOp",EDGE,"E134.MirrorC"),sQuery(id+"F0.wireOp",EDGE,"E135.MirrorCS"),sQuery(id+"F0.wireOp",EDGE,"E136.MirrorCS"),sQuery(id+"F0.wireOp",EDGE,"E137.MirrorCS"),sQuery(id+"F0.wireOp",EDGE,"E138.MirrorCS"),sQuery(id+"F0.wireOp",EDGE,"E139.MirrorCS"),sQuery(id+"F0.wireOp",EDGE,"E140.MirrorCS"),sQuery(id+"F0.wireOp",EDGE,"E141.MirrorCS"),sQuery(id+"F0.wireOp",EDGE,"E142.MirrorCS"),sQuery(id+"F0.wireOp",EDGE,"E143.MirrorCS"),sQuery(id+"F0.wireOp",EDGE,"E144.MirrorCS"),sQuery(id+"F0.wireOp",EDGE,"E145.MirrorCS"),sQuery(id+"F0.wireOp",EDGE,"E146.MirrorC"),sQuery(id+"F0.wireOp",EDGE,"E147.MirrorCS"),sQuery(id+"F0.wireOp",EDGE,"E148.MirrorCS"),sQuery(id+"F0.wireOp",EDGE,"E149.MirrorCS"),sQuery(id+"F0.wireOp",EDGE,"E150.MirrorCS"),sQuery(id+"F0.wireOp",EDGE,"E151.MirrorCS"),sQuery(id+"F0.wireOp",EDGE,"E152.MirrorCS"),sQuery(id+"F0.wireOp",EDGE,"E153.MirrorC"),sQuery(id+"F0.wireOp",EDGE,"E154.MirrorCS"),sQuery(id+"F0.wireOp",EDGE,"E155.MirrorCS"),sQuery(id+"F0.wireOp",EDGE,"E156.MirrorCS"),sQuery(id+"F0.wireOp",EDGE,"E157.MirrorCS"),sQuery(id+"F0.wireOp",EDGE,"E158.MirrorCS"),sQuery(id+"F0.wireOp",EDGE,"E159.MirrorCS"),sQuery(id+"F0.wireOp",EDGE,"E160.MirrorCS"),sQuery(id+"F0.wireOp",EDGE,"E161.MirrorCS"),sQuery(id+"F0.wireOp",EDGE,"E162.MirrorCS"),sQuery(id+"F0.wireOp",EDGE,"E163.MirrorC"),sQuery(id+"F0.wireOp",EDGE,"E164.MirrorCS"),sQuery(id+"F0.wireOp",EDGE,"E165.MirrorCS"),sQuery(id+"F0.wireOp",EDGE,"E166.MirrorCS"),sQuery(id+"F0.wireOp",EDGE,"E167.MirrorCS"),sQuery(id+"F0.wireOp",EDGE,"E168.MirrorCS"),sQuery(id+"F0.wireOp",EDGE,"E169.MirrorCS"),sQuery(id+"F0.wireOp",EDGE,"E170.MirrorCS"),sQuery(id+"F0.wireOp",EDGE,"E171.MirrorCS"),sQuery(id+"F0.wireOp",EDGE,"E172.MirrorCS"),sQuery(id+"F0.wireOp",EDGE,"E173.MirrorC"),sQuery(id+"F0.wireOp",EDGE,"E174.MirrorCS"),sQuery(id+"F0.wireOp",EDGE,"E175.MirrorCS"),sQuery(id+"F0.wireOp",EDGE,"E176.MirrorCS"),sQuery(id+"F0.wireOp",EDGE,"E177.MirrorCS"),sQuery(id+"F0.wireOp",EDGE,"E178.MirrorCS"),sQuery(id+"F0.wireOp",EDGE,"E179.MirrorCS"),sQuery(id+"F0.wireOp",EDGE,"E180.MirrorCS"),sQuery(id+"F0.wireOp",EDGE,"E181.MirrorCS"),sQuery(id+"F0.wireOp",EDGE,"E182.MirrorC"),sQuery(id+"F0.wireOp",EDGE,"E183.MirrorCS"),sQuery(id+"F0.wireOp",EDGE,"E184.MirrorCS"),sQuery(id+"F0.wireOp",EDGE,"E185.MirrorCS"),sQuery(id+"F0.wireOp",EDGE,"E186.MirrorCS"),sQuery(id+"F0.wireOp",EDGE,"E187.MirrorCS"),sQuery(id+"F0.wireOp",EDGE,"E188.MirrorCS"),sQuery(id+"F0.wireOp",EDGE,"E189.MirrorCS"),sQuery(id+"F0.wireOp",EDGE,"E190.MirrorCS"),sQuery(id+"F0.wireOp",EDGE,"E191.MirrorC"),sQuery(id+"F0.wireOp",EDGE,"E192.MirrorCS"),sQuery(id+"F0.wireOp",EDGE,"E193.MirrorCS"),sQuery(id+"F0.wireOp",EDGE,"E194.MirrorCS"),sQuery(id+"F0.wireOp",EDGE,"E195.MirrorCS"),sQuery(id+"F0.wireOp",EDGE,"E196.MirrorCS"),sQuery(id+"F0.wireOp",EDGE,"E197.MirrorCS"),sQuery(id+"F0.wireOp",EDGE,"E198.MirrorCS"),sQuery(id+"F0.wireOp",EDGE,"E199.MirrorCS"),sQuery(id+"F0.wireOp",EDGE,"E200.MirrorCS"),sQuery(id+"F0.wireOp",EDGE,"E201.MirrorC"),sQuery(id+"F0.wireOp",EDGE,"E202.MirrorCS"),sQuery(id+"F0.wireOp",EDGE,"E203.MirrorCS"),sQuery(id+"F0.wireOp",EDGE,"E204.MirrorCS"),sQuery(id+"F0.wireOp",EDGE,"E205.MirrorCS"),sQuery(id+"F0.wireOp",EDGE,"E206.MirrorCS"),sQuery(id+"F0.wireOp",EDGE,"E207.MirrorCS"),sQuery(id+"F0.wireOp",EDGE,"E208.MirrorCS"),sQuery(id+"F0.wireOp",EDGE,"E209.MirrorCS"),sQuery(id+"F0.wireOp",EDGE,"E210.MirrorC"),sQuery(id+"F0.wireOp",EDGE,"E211.MirrorCS"),sQuery(id+"F0.wireOp",EDGE,"E212.MirrorCS"),sQuery(id+"F0.wireOp",EDGE,"E213.MirrorCS"),sQuery(id+"F0.wireOp",EDGE,"E214.MirrorCS"),sQuery(id+"F0.wireOp",EDGE,"E215.MirrorCS"),sQuery(id+"F0.wireOp",EDGE,"E216.MirrorCS"),sQuery(id+"F0.wireOp",EDGE,"E217.MirrorC"),sQuery(id+"F0.wireOp",EDGE,"E218.MirrorCS"),sQuery(id+"F0.wireOp",EDGE,"E219.MirrorCS")])],"isStart":false});
            var sketch = newSketch(context, id + "F2", { "sketchPlane" : qUnion([Q0])});
            skArc(sketch, "E317.0", {"start": v(-75.41, -83.63) * mm, "mid": v(-72.64, -6.86) * mm, "end": v(3.72, -15.16) * mm});
            skLineSegment(sketch, "E317.1", {"start": v(3.72, -162.76) * mm, "end": v(-75.41, -83.63) * mm});
            skLineSegment(sketch, "E317.2", {"start": v(82.86, -83.63) * mm, "end": v(3.72, -162.76) * mm});
            skArc(sketch, "E317.3", {"start": v(82.86, -83.63) * mm, "mid": v(80.09, -6.86) * mm, "end": v(3.72, -15.16) * mm});
            skArc(sketch, "E318.0", {"start": v(-80.36, -88.57) * mm, "mid": v(-80.36, -4.49) * mm, "end": v(3.72, -4.49) * mm});
            skLineSegment(sketch, "E318.1", {"start": v(3.72, -172.66) * mm, "end": v(-80.36, -88.57) * mm});
            skLineSegment(sketch, "E318.2", {"start": v(87.8, -88.57) * mm, "end": v(3.72, -172.66) * mm});
            skArc(sketch, "E318.3", {"start": v(87.8, -88.57) * mm, "mid": v(87.8, -4.49) * mm, "end": v(3.72, -4.49) * mm});
            skSolve(sketch);
        }
        {
            var Q0;
            Q0=makeQuery(id+"F2.imprint","IMPRINT",FACE,{"disambiguationData":[TD([[makeQuery(id+"F2.imprint","IMPRINT",EDGE,{"derivedFrom":sQuery(id+"F2.wireOp",EDGE,"E317.0")}),1.0]])]});
            extrude(context, id + "F3", {"entities" : qUnion([Q0]), "depth" : 4 * mm});
        }
        {
            var Q0;
            Q0=makeQuery(id+"F0.imprint","IMPRINT",FACE,{"disambiguationData":[TD([[makeQuery(id+"F0.imprint","IMPRINT",EDGE,{"derivedFrom":sQuery(id+"F0.wireOp",EDGE,"E0")}),1.0]])]});
            var sketch = newSketch(context, id + "F4", { "sketchPlane" : qUnion([Q0])});
            skArc(sketch, "E319.0", {"start": v(-75.41, -83.63) * mm, "mid": v(-72.64, -6.87) * mm, "end": v(3.72, -15.16) * mm});
            skLineSegment(sketch, "E319.1", {"start": v(3.72, -162.77) * mm, "end": v(-75.41, -83.63) * mm});
            skLineSegment(sketch, "E319.2", {"start": v(82.86, -83.63) * mm, "end": v(3.72, -162.77) * mm});
            skArc(sketch, "E319.3", {"start": v(82.86, -83.63) * mm, "mid": v(80.09, -6.87) * mm, "end": v(3.72, -15.16) * mm});
            skArc(sketch, "E320.0", {"start": v(-80.36, -88.58) * mm, "mid": v(-80.36, -4.5) * mm, "end": v(3.72, -4.5) * mm});
            skLineSegment(sketch, "E320.1", {"start": v(3.72, -172.66) * mm, "end": v(-80.36, -88.58) * mm});
            skLineSegment(sketch, "E320.2", {"start": v(87.8, -88.58) * mm, "end": v(3.72, -172.66) * mm});
            skArc(sketch, "E320.3", {"start": v(87.8, -88.58) * mm, "mid": v(87.8, -4.5) * mm, "end": v(3.72, -4.5) * mm});
            skSolve(sketch);
        }
        {
            var Q0;
            Q0=makeQuery(id+"F4.imprint","IMPRINT",FACE,{"disambiguationData":[TD([[makeQuery(id+"F4.imprint","IMPRINT",EDGE,{"derivedFrom":sQuery(id+"F4.wireOp",EDGE,"E319.0")}),1.0]])]});
            extrude(context, id + "F5", {"entities" : qUnion([Q0]), "oppositeDirection" : true, "depth" : 4 * mm});
        }
    });
